# Revit family: Urinal-Wall_Mount-KOHLER-PATIO-K-18645IN-1
name_source: partatom
category: Plumbing Fixtures
units: mm (PartAtom-declared; Revit-internal decimal feet)

## family parameters
Cut with Voids When Loaded = No
Host = Face
OmniClass Number = 23.31.21.00
OmniClass Title = Urinals
Part Type = Normal
Room Calculation Point = No
Round Connector Dimension = Use Diameter
Shared = No

## types (2) — shared parameters
ADA Compliant = No
Assembly Code = D2010200
CW Connection = Yes
Cold Water Inlet = Cold Water Inlet
Date Modified = 05/25/2024
Default Elevation = 0"
Description = Urinal 0.5L anti-microbial(rear)
Flow Rate = 0 GPM
Flush Rate- GPF = 0.13 GPF
Flush Rate- LPF = 0.5 LPF
HW Connection = No
Height = 25 1/4"
Hot Water Inlet = Hot Water Inlet
Length = 13 3/16"
Manufacturer = KOHLER Co.
Master Format 2014 = 22 41 13.16
Master Format 2014 Name = Residential Urinals
Material = Vitreous China
Pressure = 0.00 psi
Product Name = PATIO
URL = https://www.kohler.co.in
Vent Connection = No
Waste Connection = Yes
Waste Water Outlet = Waste Water Outlet
WaterSense Certified = No
Width = 13 3/16"

## per-type parameters (varying)
| type | Finish | Model | Product Page URL | Type |
| 0-White | Kohler-Vitreous_China-0-White | K-18645IN-SS-0 | https://www.kohler.co.in | 1 |
| 7-Black Black | Kohler-Vitreous_China-7-Black_Black | K-18645IN-SS-7 |  | 2 |

## geometry (parser evidence)
native form markers: Sweep x5
no freeform markers — native parametric forms only
